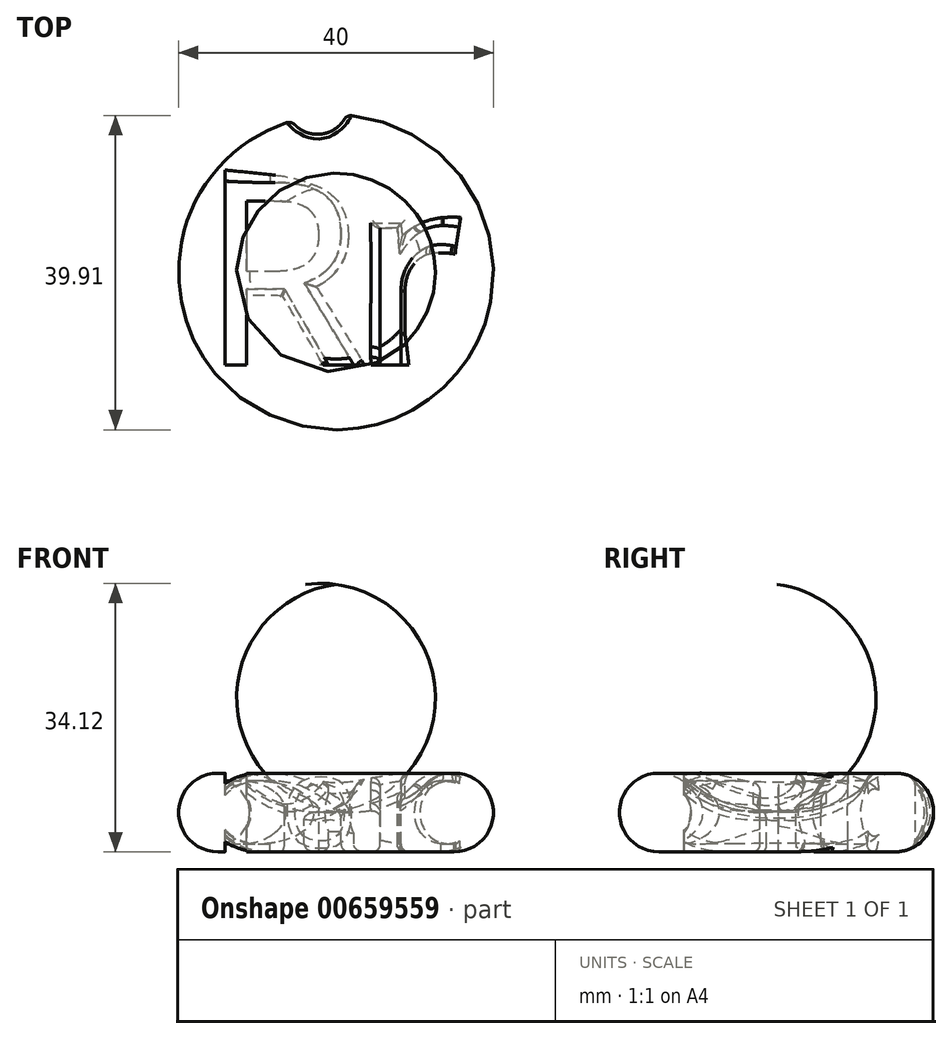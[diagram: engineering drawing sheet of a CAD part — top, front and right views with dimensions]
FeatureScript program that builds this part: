
annotation { "Feature Type Name" : "Feature", "Feature Type Description" : "" }
export const myFeature = defineFeature(function(context is Context, id is Id, definition is map)
    precondition{}
    {
        {
            var Q0;
            Q0=qCreatedBy(makeId("Front.planeOp"),FACE);
            var sketch = newSketch(context, id + "F0", { "sketchPlane" : qUnion([Q0])});
            skArc(sketch, "E0", {"start": v(-11.66, 8.72) * mm, "mid": v(-19.67, 6.79) * mm, "end": v(-15, 0) * mm});
            skArc(sketch, "E1", {"start": v(-11.66, 8.72) * mm, "mid": v(-6.23, 5.65) * mm, "end": v(0, 5.13) * mm});
            skLineSegment(sketch, "E2", {"start": v(-15, 0) * mm, "end": v(0, 0) * mm});
            skLineSegment(sketch, "E3", {"start": v(0, 0) * mm, "end": v(0, 5.13) * mm});
            skSolve(sketch);
        }
        {
            var Q0;
            Q0=makeQuery(id+"F0.imprint","IMPRINT",FACE,{"disambiguationData":[TD([[makeQuery(id+"F0.imprint","IMPRINT",EDGE,{"derivedFrom":sQuery(id+"F0.wireOp",EDGE,"E0")}),1.0]])]});
            var Q1;
            Q1=sQuery(id+"F0.wireOp",EDGE,"E3");
            revolve(context, id + "F1", {"entities" : qUnion([Q0]), "axis" : qUnion([Q1]), "revolveType" : RevolveType.FULL});
        }
        {
            var Q0;
            Q0=qCreatedBy(makeId("Top.planeOp"),FACE);
            cPlane(context, id + "F2", {"entities" : qUnion([Q0]), "cplaneType" : CPlaneType.OFFSET, "offset" : 40 * mm, "width" : 150 * mm, "height" : 150 * mm});
        }
        {
            var Q0;
            Q0=qCreatedBy(id+"F2.planeOp",FACE);
            var sketch = newSketch(context, id + "F3", { "sketchPlane" : qUnion([Q0])});
            skText(sketch, "E4", { "text": "Rr", "fontName": "OpenSans-Regular.ttf"});
            const initialGuessF3  = {"E4": [-0.01727, -0.01178, 1, 0, 0.0234]};
            skSetInitialGuess(sketch, initialGuessF3);
            skSolve(sketch);
        }
        {
            var Q0;
            Q0=makeQuery(id+"F3.imprint","IMPRINT",FACE,{"disambiguationData":[TD([[makeQuery(id+"F3.imprint","IMPRINT",EDGE,{"derivedFrom":sQuery(id+"F3.wireOp",EDGE,"E4.sketch_text.stroke-0")}),-1.0]])]});
            var Q1;
            Q1=makeQuery(id+"F3.imprint","IMPRINT",FACE,{"disambiguationData":[TD([[makeQuery(id+"F3.imprint","IMPRINT",EDGE,{"derivedFrom":sQuery(id+"F3.wireOp",EDGE,"E4.sketch_text.stroke-18")}),-1.0]])]});
            extrude(context, id + "F4", {"entities" : qUnion([Q0, Q1]), "operationType" : NewBodyOperationType.REMOVE, "oppositeDirection" : true, "depth" : 100 * mm, "offsetDistance" : 25 * mm});
        }
        {
            var Q0;
            Q0=qCreatedBy(makeId("Front.planeOp"),FACE);
            var sketch = newSketch(context, id + "F5", { "sketchPlane" : qUnion([Q0])});
            skCircle(sketch, "E5", {"center": v(-15, 5) * mm, "radius": 4 * mm});
            skSolve(sketch);
        }
        {
            var Q0;
            Q0 = qSketchRegion(id + "F5", true);
            var Q1;
            Q1=sQuery(id+"F0.wireOp",EDGE,"E3");
            revolve(context, id + "F6", {"operationType" : NewBodyOperationType.ADD, "entities" : qUnion([Q0]), "axis" : qUnion([Q1]), "revolveType" : RevolveType.FULL});
        }
        {
            var Q0;
            Q0=qCreatedBy(makeId("Top.planeOp"),FACE);
            var sketch = newSketch(context, id + "F7", { "sketchPlane" : qUnion([Q0])});
            skCircle(sketch, "E6", {"center": v(-2.36, 21.54) * mm, "radius": 4 * mm});
            skSolve(sketch);
        }
        {
            var Q0;
            Q0=makeQuery(id+"F7.imprint","IMPRINT",FACE,{"disambiguationData":[TD([[makeQuery(id+"F7.imprint","IMPRINT",EDGE,{"derivedFrom":sQuery(id+"F7.wireOp",EDGE,"E6")}),1.0]])]});
            extrude(context, id + "F8", {"entities" : qUnion([Q0]), "operationType" : NewBodyOperationType.REMOVE, "depth" : 25 * mm, "offsetDistance" : 25 * mm});
        }
        {
            var Q0;
            Q0=makeQuery(id+"F8.boolean.opBoolean","INTERSECT",EDGE,{"derivedFrom":[makeQuery(id+"F4.boolean.opBoolean","SPLIT",FACE,{"disambiguationData":[TD([makeQuery(id+"F1.opRevolve","SWEPT_FACE",FACE,{"disambiguationData":[OSD([sQuery(id+"F0.wireOp",EDGE,"E2")])]})])],"derivedFrom":makeQuery(id+"F1.opRevolve","SWEPT_FACE",FACE,{"disambiguationData":[OSD([sQuery(id+"F0.wireOp",EDGE,"E0")])]})}),makeQuery(id+"F8.opExtrude","SWEPT_FACE",FACE,{"disambiguationData":[OSD([sQuery(id+"F7.wireOp",EDGE,"E6")])]})]});
            fillet(context, id + "F9", {"entities" : qUnion([Q0]), "radius" : 1 * mm, "tangentPropagation" : true, "allowEdgeOverflow" : false});
        }
        {
            var Q0;
            Q0=makeQuery(id+"F4.boolean.opBoolean","INTERSECT",EDGE,{"derivedFrom":[makeQuery(id+"F1.opRevolve","SWEPT_FACE",FACE,{"disambiguationData":[OSD([sQuery(id+"F0.wireOp",EDGE,"E1")])]}),makeQuery(id+"F4.opExtrude","SWEPT_FACE",FACE,{"disambiguationData":[OSD([sQuery(id+"F3.wireOp",EDGE,"E4.sketch_text.stroke-9")])]})]});
            var Q1;
            Q1=makeQuery(id+"F4.boolean.opBoolean","INTERSECT",EDGE,{"derivedFrom":[makeQuery(id+"F1.opRevolve","SWEPT_FACE",FACE,{"disambiguationData":[OSD([sQuery(id+"F0.wireOp",EDGE,"E1")])]}),makeQuery(id+"F4.opExtrude","SWEPT_FACE",FACE,{"disambiguationData":[OSD([sQuery(id+"F3.wireOp",EDGE,"E4.sketch_text.stroke-10")])]})]});
            var Q2;
            Q2=makeQuery(id+"F4.boolean.opBoolean","INTERSECT",EDGE,{"derivedFrom":[makeQuery(id+"F1.opRevolve","SWEPT_FACE",FACE,{"disambiguationData":[OSD([sQuery(id+"F0.wireOp",EDGE,"E2")])]}),makeQuery(id+"F4.opExtrude","SWEPT_FACE",FACE,{"disambiguationData":[OSD([sQuery(id+"F3.wireOp",EDGE,"E4.sketch_text.stroke-9")])]})]});
            var Q3;
            Q3=makeQuery(id+"F4.boolean.opBoolean","INTERSECT",EDGE,{"derivedFrom":[makeQuery(id+"F1.opRevolve","SWEPT_FACE",FACE,{"disambiguationData":[OSD([sQuery(id+"F0.wireOp",EDGE,"E2")])]}),makeQuery(id+"F4.opExtrude","SWEPT_FACE",FACE,{"disambiguationData":[OSD([sQuery(id+"F3.wireOp",EDGE,"E4.sketch_text.stroke-10")])]})]});
            var Q4;
            Q4=makeQuery(id+"F4.boolean.opBoolean","INTERSECT",EDGE,{"derivedFrom":[makeQuery(id+"F1.opRevolve","SWEPT_FACE",FACE,{"disambiguationData":[OSD([sQuery(id+"F0.wireOp",EDGE,"E1")])]}),makeQuery(id+"F4.opExtrude","SWEPT_FACE",FACE,{"disambiguationData":[OSD([sQuery(id+"F3.wireOp",EDGE,"E4.sketch_text.stroke-7")])]})]});
            var Q5;
            Q5=makeQuery(id+"F4.boolean.opBoolean","INTERSECT",EDGE,{"derivedFrom":[makeQuery(id+"F1.opRevolve","SWEPT_FACE",FACE,{"disambiguationData":[OSD([sQuery(id+"F0.wireOp",EDGE,"E2")])]}),makeQuery(id+"F4.opExtrude","SWEPT_FACE",FACE,{"disambiguationData":[OSD([sQuery(id+"F3.wireOp",EDGE,"E4.sketch_text.stroke-7")])]})]});
            var Q6;
            Q6=makeQuery(id+"F4.boolean.opBoolean","INTERSECT",EDGE,{"derivedFrom":[makeQuery(id+"F1.opRevolve","SWEPT_FACE",FACE,{"disambiguationData":[OSD([sQuery(id+"F0.wireOp",EDGE,"E1")])]}),makeQuery(id+"F4.opExtrude","SWEPT_FACE",FACE,{"disambiguationData":[OSD([sQuery(id+"F3.wireOp",EDGE,"E4.sketch_text.stroke-25")])]})]});
            var Q7;
            Q7=makeQuery(id+"F4.boolean.opBoolean","INTERSECT",EDGE,{"derivedFrom":[makeQuery(id+"F1.opRevolve","SWEPT_FACE",FACE,{"disambiguationData":[OSD([sQuery(id+"F0.wireOp",EDGE,"E2")])]}),makeQuery(id+"F4.opExtrude","SWEPT_FACE",FACE,{"disambiguationData":[OSD([sQuery(id+"F3.wireOp",EDGE,"E4.sketch_text.stroke-25")])]})]});
            var Q8;
            Q8=makeQuery(id+"F4.boolean.opBoolean","INTERSECT",EDGE,{"derivedFrom":[makeQuery(id+"F1.opRevolve","SWEPT_FACE",FACE,{"disambiguationData":[OSD([sQuery(id+"F0.wireOp",EDGE,"E2")])]}),makeQuery(id+"F4.opExtrude","SWEPT_FACE",FACE,{"disambiguationData":[OSD([sQuery(id+"F3.wireOp",EDGE,"E4.sketch_text.stroke-23")])]})]});
            var Q9;
            Q9=makeQuery(id+"F4.boolean.opBoolean","INTERSECT",EDGE,{"derivedFrom":[makeQuery(id+"F1.opRevolve","SWEPT_FACE",FACE,{"disambiguationData":[OSD([sQuery(id+"F0.wireOp",EDGE,"E1")])]}),makeQuery(id+"F4.opExtrude","SWEPT_FACE",FACE,{"disambiguationData":[OSD([sQuery(id+"F3.wireOp",EDGE,"E4.sketch_text.stroke-23")])]})]});
            var Q10;
            Q10=makeQuery(id+"F4.boolean.opBoolean","INTERSECT",EDGE,{"derivedFrom":[makeQuery(id+"F1.opRevolve","SWEPT_FACE",FACE,{"disambiguationData":[OSD([sQuery(id+"F0.wireOp",EDGE,"E2")])]}),makeQuery(id+"F4.opExtrude","SWEPT_FACE",FACE,{"disambiguationData":[OSD([sQuery(id+"F3.wireOp",EDGE,"E4.sketch_text.stroke-27")])]})]});
            var Q11;
            Q11=makeQuery(id+"F4.boolean.opBoolean","INTERSECT",EDGE,{"derivedFrom":[makeQuery(id+"F1.opRevolve","SWEPT_FACE",FACE,{"disambiguationData":[OSD([sQuery(id+"F0.wireOp",EDGE,"E2")])]}),makeQuery(id+"F4.opExtrude","SWEPT_FACE",FACE,{"disambiguationData":[OSD([sQuery(id+"F3.wireOp",EDGE,"E4.sketch_text.stroke-26")])]})]});
            var Q12;
            Q12=makeQuery(id+"F4.boolean.opBoolean","INTERSECT",EDGE,{"derivedFrom":[makeQuery(id+"F1.opRevolve","SWEPT_FACE",FACE,{"disambiguationData":[OSD([sQuery(id+"F0.wireOp",EDGE,"E1")])]}),makeQuery(id+"F4.opExtrude","SWEPT_FACE",FACE,{"disambiguationData":[OSD([sQuery(id+"F3.wireOp",EDGE,"E4.sketch_text.stroke-27")])]})]});
            var Q13;
            Q13=makeQuery(id+"F4.boolean.opBoolean","INTERSECT",EDGE,{"derivedFrom":[makeQuery(id+"F1.opRevolve","SWEPT_FACE",FACE,{"disambiguationData":[OSD([sQuery(id+"F0.wireOp",EDGE,"E1")])]}),makeQuery(id+"F4.opExtrude","SWEPT_FACE",FACE,{"disambiguationData":[OSD([sQuery(id+"F3.wireOp",EDGE,"E4.sketch_text.stroke-26")])]})]});
            var Q14;
            Q14=makeQuery(id+"F4.boolean.opBoolean","INTERSECT",EDGE,{"derivedFrom":[makeQuery(id+"F1.opRevolve","SWEPT_FACE",FACE,{"disambiguationData":[OSD([sQuery(id+"F0.wireOp",EDGE,"E1")])]}),makeQuery(id+"F4.opExtrude","SWEPT_FACE",FACE,{"disambiguationData":[OSD([sQuery(id+"F3.wireOp",EDGE,"E4.sketch_text.stroke-29")])]})]});
            var Q15;
            Q15=makeQuery(id+"F4.boolean.opBoolean","INTERSECT",EDGE,{"derivedFrom":[makeQuery(id+"F1.opRevolve","SWEPT_FACE",FACE,{"disambiguationData":[OSD([sQuery(id+"F0.wireOp",EDGE,"E1")])]}),makeQuery(id+"F4.opExtrude","SWEPT_FACE",FACE,{"disambiguationData":[OSD([sQuery(id+"F3.wireOp",EDGE,"E4.sketch_text.stroke-6")])]})]});
            var Q16;
            Q16=makeQuery(id+"F4.boolean.opBoolean","INTERSECT",EDGE,{"derivedFrom":[makeQuery(id+"F1.opRevolve","SWEPT_FACE",FACE,{"disambiguationData":[OSD([sQuery(id+"F0.wireOp",EDGE,"E2")])]}),makeQuery(id+"F4.opExtrude","SWEPT_FACE",FACE,{"disambiguationData":[OSD([sQuery(id+"F3.wireOp",EDGE,"E4.sketch_text.stroke-5")])]})]});
            var Q17;
            Q17=makeQuery(id+"F4.boolean.opBoolean","INTERSECT",EDGE,{"derivedFrom":[makeQuery(id+"F1.opRevolve","SWEPT_FACE",FACE,{"disambiguationData":[OSD([sQuery(id+"F0.wireOp",EDGE,"E2")])]}),makeQuery(id+"F4.opExtrude","SWEPT_FACE",FACE,{"disambiguationData":[OSD([sQuery(id+"F3.wireOp",EDGE,"E4.sketch_text.stroke-30")])]})]});
            fillet(context, id + "F10", {"entities" : qUnion([Q0, Q1, Q2, Q3, Q4, Q5, Q6, Q7, Q8, Q9, Q10, Q11, Q12, Q13, Q14, Q15, Q16, Q17]), "radius" : 1 * mm, "tangentPropagation" : true, "allowEdgeOverflow" : false});
        }
    });
